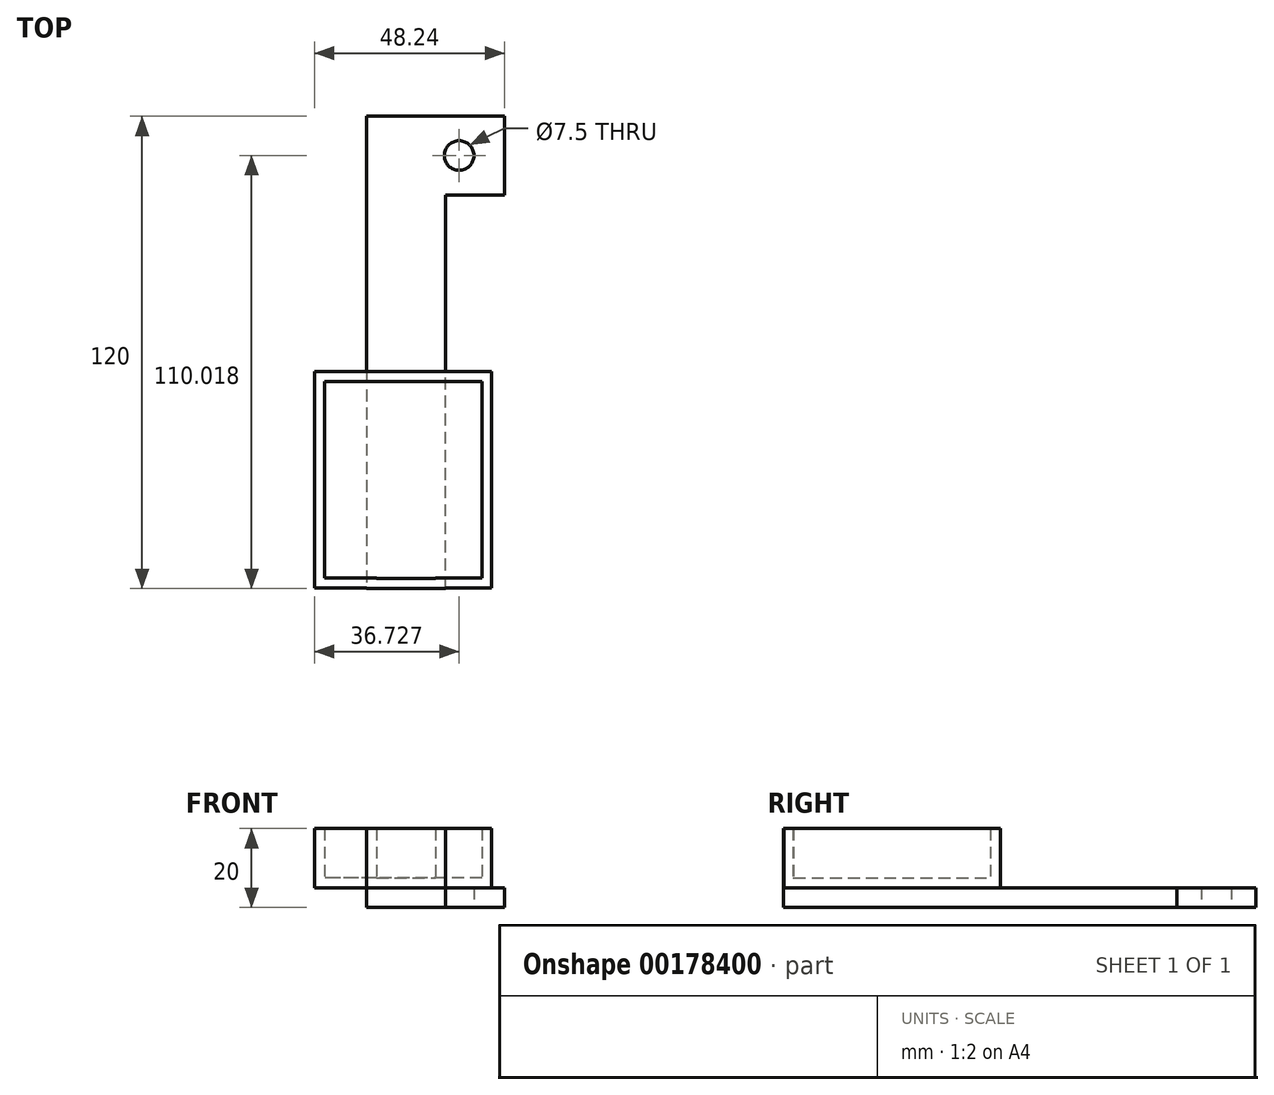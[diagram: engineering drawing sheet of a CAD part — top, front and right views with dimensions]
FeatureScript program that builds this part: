
annotation { "Feature Type Name" : "Feature", "Feature Type Description" : "" }
export const myFeature = defineFeature(function(context is Context, id is Id, definition is map)
    precondition{}
    {
        {
            var Q0;
            Q0=qCreatedBy(makeId("Top.planeOp"),FACE);
            var sketch = newSketch(context, id + "F0", { "sketchPlane" : qUnion([Q0])});
            skLineSegment(sketch, "E0", {"start": v(-34.8, -1.67) * mm, "end": v(-34.8, -34.83) * mm});
            skLineSegment(sketch, "E1", {"start": v(-34.8, -34.83) * mm, "end": v(-14.8, -34.83) * mm});
            skLineSegment(sketch, "E2", {"start": v(-14.8, -34.83) * mm, "end": v(-14.8, 65.17) * mm});
            skLineSegment(sketch, "E3", {"start": v(-14.8, 65.17) * mm, "end": v(0.2, 65.17) * mm});
            skLineSegment(sketch, "E4", {"start": v(0.2, 65.17) * mm, "end": v(0.2, 85.17) * mm});
            skLineSegment(sketch, "E5", {"start": v(0.2, 85.17) * mm, "end": v(-34.8, 85.17) * mm});
            skLineSegment(sketch, "E6", {"start": v(-34.8, 85.17) * mm, "end": v(-34.8, -1.67) * mm});
            skSolve(sketch);
        }
        {
            var Q0;
            Q0=makeQuery(id+"F0.imprint","IMPRINT",FACE,{"disambiguationData":[TD([[makeQuery(id+"F0.imprint","IMPRINT",EDGE,{"derivedFrom":sQuery(id+"F0.wireOp",EDGE,"E0")}),1.0]])]});
            extrude(context, id + "F1", {"entities" : qUnion([Q0]), "endBound" : BoundingType.SYMMETRIC, "depth" : 5 * mm});
        }
        {
            var Q0;
            Q0=makeQuery(id+"F1.opExtrude","CAP_FACE",FACE,{"disambiguationData":[OSD([sQuery(id+"F0.wireOp",EDGE,"E0"),sQuery(id+"F0.wireOp",EDGE,"E1"),sQuery(id+"F0.wireOp",EDGE,"E2"),sQuery(id+"F0.wireOp",EDGE,"E3"),sQuery(id+"F0.wireOp",EDGE,"E4"),sQuery(id+"F0.wireOp",EDGE,"E5"),sQuery(id+"F0.wireOp",EDGE,"E6")])],"isStart":false});
            var sketch = newSketch(context, id + "F2", { "sketchPlane" : qUnion([Q0])});
            skLineSegment(sketch, "E7.bottom", {"start": v(-3.05, -34.68) * mm, "end": v(-48.05, -34.68) * mm});
            skLineSegment(sketch, "E7.top", {"start": v(-3.05, 20.32) * mm, "end": v(-48.05, 20.32) * mm});
            skLineSegment(sketch, "E7.left", {"start": v(-3.05, -34.68) * mm, "end": v(-3.05, 20.32) * mm});
            skLineSegment(sketch, "E7.right", {"start": v(-48.05, -34.68) * mm, "end": v(-48.05, 20.32) * mm});
            skPoint(sketch, "E7.middle", {"position": v(-25.55, -7.18) * mm});
            skSolve(sketch);
        }
        {
            var Q0;
            {var subQ5=makeQuery(id+"F1.opExtrude","CAP_EDGE",EDGE,{"disambiguationData":[OSD([sQuery(id+"F0.wireOp",EDGE,"E1")])],"isStart":false});Q0=makeQuery(id+"F2.imprint","IMPRINT",FACE,{"disambiguationData":[TD([[makeQuery(id+"F2.imprint","IMPRINT",EDGE,{"derivedFrom":subQ5}),1.0]])]});}
            var Q1;
            Q1=makeQuery(id+"F2.imprint","IMPRINT",FACE,{"disambiguationData":[TD([[makeQuery(id+"F2.imprint","IMPRINT",EDGE,{"derivedFrom":sQuery(id+"F2.wireOp",EDGE,"E7.bottom")}),-1.0]])]});
            extrude(context, id + "F3", {"entities" : qUnion([Q0, Q1]), "depth" : 15 * mm});
        }
        {
            var Q0;
            Q0=makeQuery(id+"F3.opExtrude","CAP_FACE",FACE,{"disambiguationData":[OSD([sQuery(id+"F2.wireOp",EDGE,"E7.bottom"),sQuery(id+"F2.wireOp",EDGE,"E7.top"),sQuery(id+"F2.wireOp",EDGE,"E7.left"),sQuery(id+"F2.wireOp",EDGE,"E7.right")])],"isStart":false});
            shell(context, id + "F4", {"entities" : qUnion([Q0]), "thickness" : 2.5 * mm});
        }
        {
            var Q0;
            Q0=qCreatedBy(makeId("Top.planeOp"),FACE);
            var sketch = newSketch(context, id + "F5", { "sketchPlane" : qUnion([Q0])});
            skCircle(sketch, "E8", {"center": v(-11.32, 75.19) * mm, "radius": 3.75 * mm});
            skSolve(sketch);
        }
        {
            var Q0;
            Q0 = qSketchRegion(id + "F5", true);
            extrude(context, id + "F6", {"entities" : qUnion([Q0]), "operationType" : NewBodyOperationType.REMOVE, "endBound" : BoundingType.SYMMETRIC, "depth" : 10 * mm});
        }
    });
